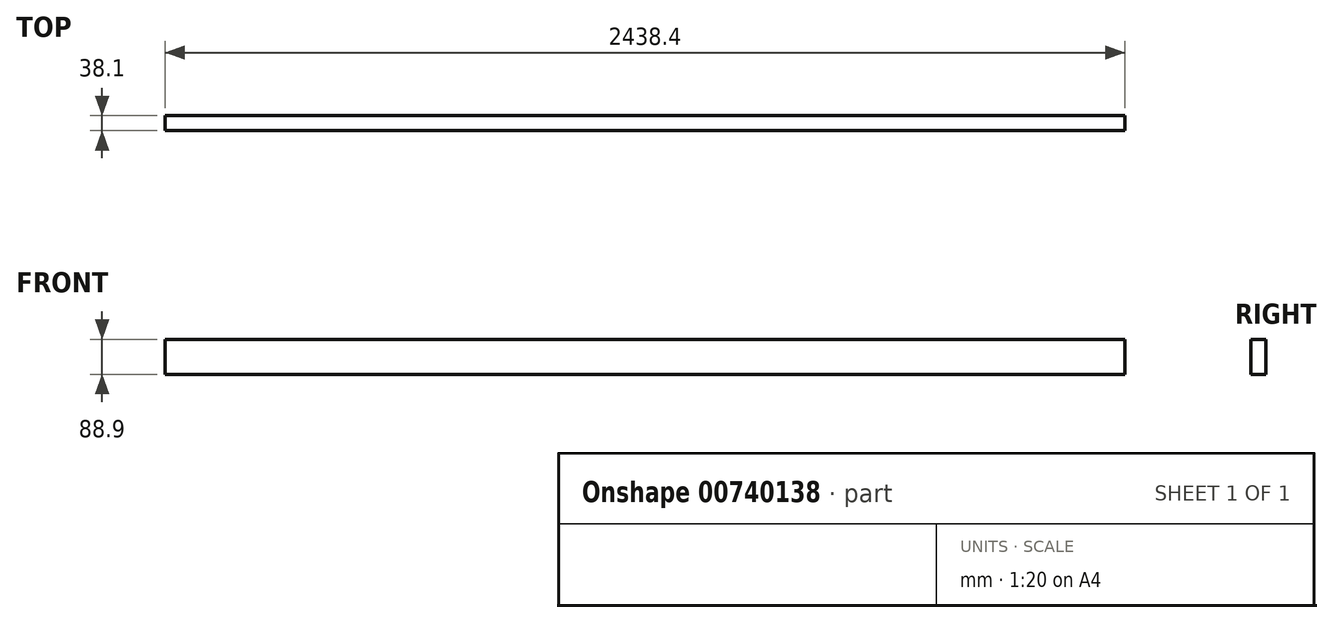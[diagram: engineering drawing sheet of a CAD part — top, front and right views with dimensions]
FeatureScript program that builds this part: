
annotation { "Feature Type Name" : "Feature", "Feature Type Description" : "" }
export const myFeature = defineFeature(function(context is Context, id is Id, definition is map)
    precondition{}
    {
        {
            var Q0;
            Q0=qCreatedBy(makeId("Right.planeOp"),FACE);
            var sketch = newSketch(context, id + "F0", { "sketchPlane" : qUnion([Q0])});
            skLineSegment(sketch, "E0.bottom", {"start": v(-79.68, 85.36) * mm, "end": v(-41.58, 85.36) * mm});
            skLineSegment(sketch, "E0.top", {"start": v(-79.68, -3.54) * mm, "end": v(-41.58, -3.54) * mm});
            skLineSegment(sketch, "E0.left", {"start": v(-79.68, 85.36) * mm, "end": v(-79.68, -3.54) * mm});
            skLineSegment(sketch, "E0.right", {"start": v(-41.58, 85.36) * mm, "end": v(-41.58, -3.54) * mm});
            skSolve(sketch);
        }
        {
            var Q0;
            Q0=makeQuery(id+"F0.imprint","IMPRINT",FACE,{"disambiguationData":[TD([[makeQuery(id+"F0.imprint","IMPRINT",EDGE,{"derivedFrom":sQuery(id+"F0.wireOp",EDGE,"E0.bottom")}),-1.0]])]});
            extrude(context, id + "F1", {"entities" : qUnion([Q0]), "depth" : 2438.4 * mm, "offsetDistance" : 25.4 * mm});
        }
    });
